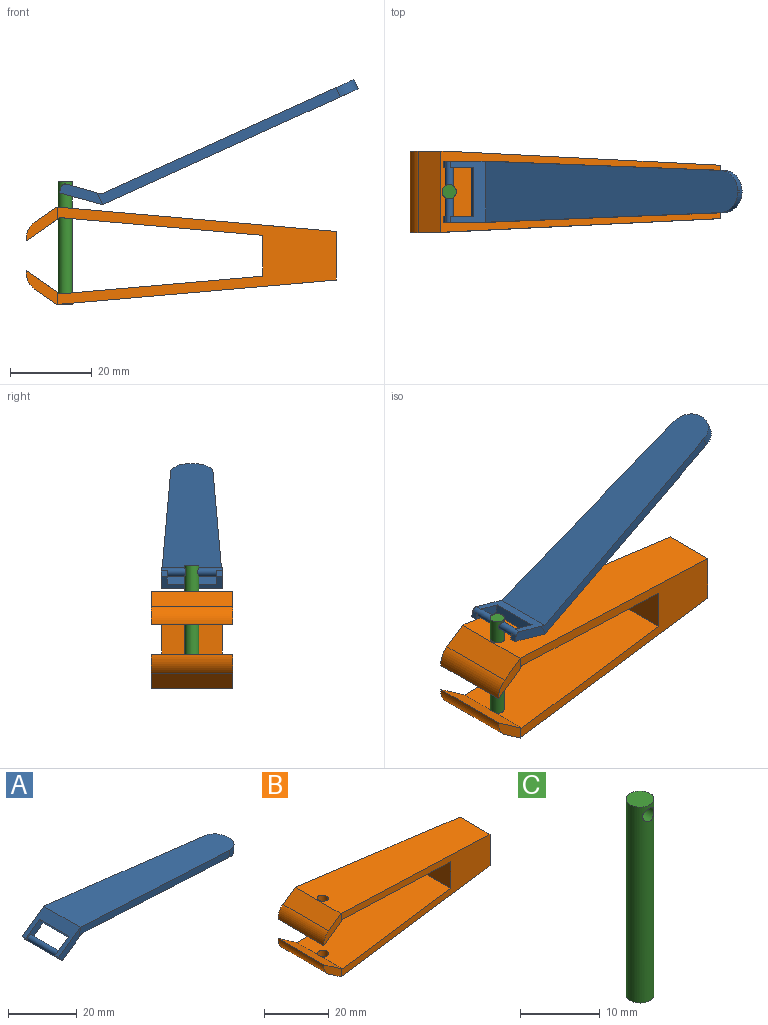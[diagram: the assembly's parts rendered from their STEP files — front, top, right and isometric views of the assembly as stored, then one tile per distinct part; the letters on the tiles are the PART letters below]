
ASSEMBLY  parts=3 mates=2
PART A: 17 faces, bbox 77.4x15x8.5 mm
  f0: plane 1.5x1.23mm, normal (-0.82,0,-0.57), area 2.3mm2, adj f2,f5,f15,f16
  f1: plane 15x7.37mm, normal (0.57,0,-0.82), area 63mm2, adj f4,f5,f7,f8,f10,f13,f14,f15
  f2: plane 15x8.94mm, normal (-0.57,0,0.82), area 79.6mm2, adj f0,f3,f4,f5,f6,f13,f14,f15
  f3: plane 68.46x15mm, normal (0.09,0,1), area 849.1mm2, adj f2,f8,f9,f10,f11,f12
  f4: plane 8.94x7.91mm, normal (0,-1,0), area 24.4mm2, adj f1,f2,f6,f10,f16
  f5: plane 8.94x7.91mm, normal (0,1,0), area 24.4mm2, adj f0,f1,f2,f8,f16
  f6: plane 1.5x1.23mm, normal (-0.82,0,-0.57), area 2.3mm2, adj f2,f4,f13,f16
  f7: plane 67.55x14.93mm, normal (-0.09,0,-1), area 835.5mm2, adj f1,f8,f9,f10,f11,f12
  f8: plane 63.94x8.06mm, normal (0.04,1,0), area 160.2mm2, adj f1,f3,f5,f7,f11
  f9: plane 2.49x0.36mm, normal (1,0,-0.09), area 0.9mm2, adj f3,f7,f11,f12
  f10: plane 63.94x8.06mm, normal (0.04,-1,0), area 160.2mm2, adj f1,f3,f4,f7,f12
  f11: cylinder r=5mm len=5.02mm, axis (-0.09,0,-1), area 19.2mm2, adj f3,f7,f8,f9
  f12: cylinder r=5mm len=5.02mm, axis (0.09,0,1), area 19.2mm2, adj f3,f7,f9,f10
  f13: plane 7.17x5.49mm, normal (0,1,0), area 14.1mm2, adj f1,f2,f6,f14,f16
  f14: plane 12x2.05mm, normal (-0.82,0,-0.57), area 30mm2, adj f1,f2,f13,f15
  f15: plane 7.17x5.49mm, normal (0,-1,0), area 14.1mm2, adj f0,f1,f2,f14,f16
  f16: cylinder r=1mm len=15mm, axis (0,-1,0), area 80.1mm2, adj f0,f1,f4,f5,f6,f13,f15
PART B: 22 faces, bbox 76x20x23.9 mm
  f0: plane 68.46x20mm, normal (0.09,0,1), area 1124mm2, adj f6,f7,f8,f11,f14,f15,f16,f19
  f1: plane 20x8.19mm, normal (0.57,0,-0.82), area 199.2mm2, adj f2,f6,f7,f15,f16,f19,f20
  f2: plane 49.81x19.85mm, normal (-0.09,0,-1), area 859.1mm2, adj f1,f7,f9,f14,f15,f19
  f3: plane 49.81x19.85mm, normal (-0.09,0,1), area 859.1mm2, adj f4,f9,f13,f14,f15,f18
  f4: plane 20x8.19mm, normal (0.57,0,0.82), area 199.2mm2, adj f3,f12,f13,f15,f17,f18,f21
  f5: plane 68.46x20mm, normal (0.09,0,-1), area 1124mm2, adj f10,f11,f12,f13,f14,f15,f17,f18
  f6: plane 8.31x7.65mm, normal (0,-1,0), area 22.3mm2, adj f0,f1,f8,f16,f20
  f7: plane 8.42x8.31mm, normal (0,1,0), area 24.4mm2, adj f0,f1,f2,f8,f14,f20
  f8: plane 20x5.39mm, normal (-0.57,0,0.82), area 131.6mm2, adj f0,f6,f7,f20
  f9: plane 14.87x10mm, normal (-1,0,0), area 148.7mm2, adj f2,f3,f14,f15
  f10: plane 20x5.39mm, normal (-0.57,0,-0.82), area 131.6mm2, adj f5,f12,f13,f21
  f11: plane 13.06x11.88mm, normal (1,0,0), area 155.1mm2, adj f0,f5,f14,f15
  f12: plane 8.31x7.65mm, normal (0,-1,0), area 22.3mm2, adj f4,f5,f10,f17,f21
  f13: plane 8.42x8.31mm, normal (0,1,0), area 24.4mm2, adj f3,f4,f5,f10,f14,f21
  f14: plane 67.56x23.7mm, normal (0.05,1,0), area 491.1mm2, adj f0,f2,f3,f5,f7,f9,f11,f13
  f15: plane 68.33x23.83mm, normal (0.05,-1,0), area 495.2mm2, adj f0,f1,f2,f3,f4,f5,f9,f11
  f16: plane 2.95x0.12mm, normal (1,0,0), area 0.4mm2, adj f0,f1,f6,f15
  f17: plane 2.95x0.12mm, normal (1,0,0), area 0.4mm2, adj f4,f5,f12,f15
  f18: cylinder r=1.75mm len=3.5mm, axis (0,0,-1), area 28mm2, adj f3,f4,f5
  f19: cylinder r=1.75mm len=3.5mm, axis (0,0,-1), area 28mm2, adj f0,f1,f2
  f20: cylinder r=5mm len=20mm, axis (0,1,0), area 104.7mm2, adj f1,f6,f7,f8
  f21: cylinder r=5mm len=20mm, axis (0,1,0), area 104.7mm2, adj f4,f10,f12,f13
PART C: 4 faces, bbox 3.5x3.5x30 mm
  f0: plane 3.5x3.5mm, normal (0,0,1), area 9.6mm2, adj f2
  f1: plane 3.5x3.5mm, normal (0,0,-1), area 9.6mm2, adj f2
  f2: cylinder r=1.75mm len=30mm, axis (0,0,1), area 323.3mm2, adj f0,f1,f3
  f3: cylinder r=1mm len=3.5mm, axis (0,-1,0), area 20.1mm2, adj f2
PLACE A rot(axis=(0.99,0,0.17),180deg) t=(-0.47,9.13,131.4)mm
PLACE B t=(-25.4,9.09,56.59)mm
PLACE C t=(-23.45,9.13,89.48)mm
MATE revolute A.f16 <-> C.f3  axis (0,1,0) through (-23.45,9.13,117.98)mm
MATE fastened C.f2 <-> B.f18  axis (0,0,-1) through (-23.45,9.13,89.48)mm
